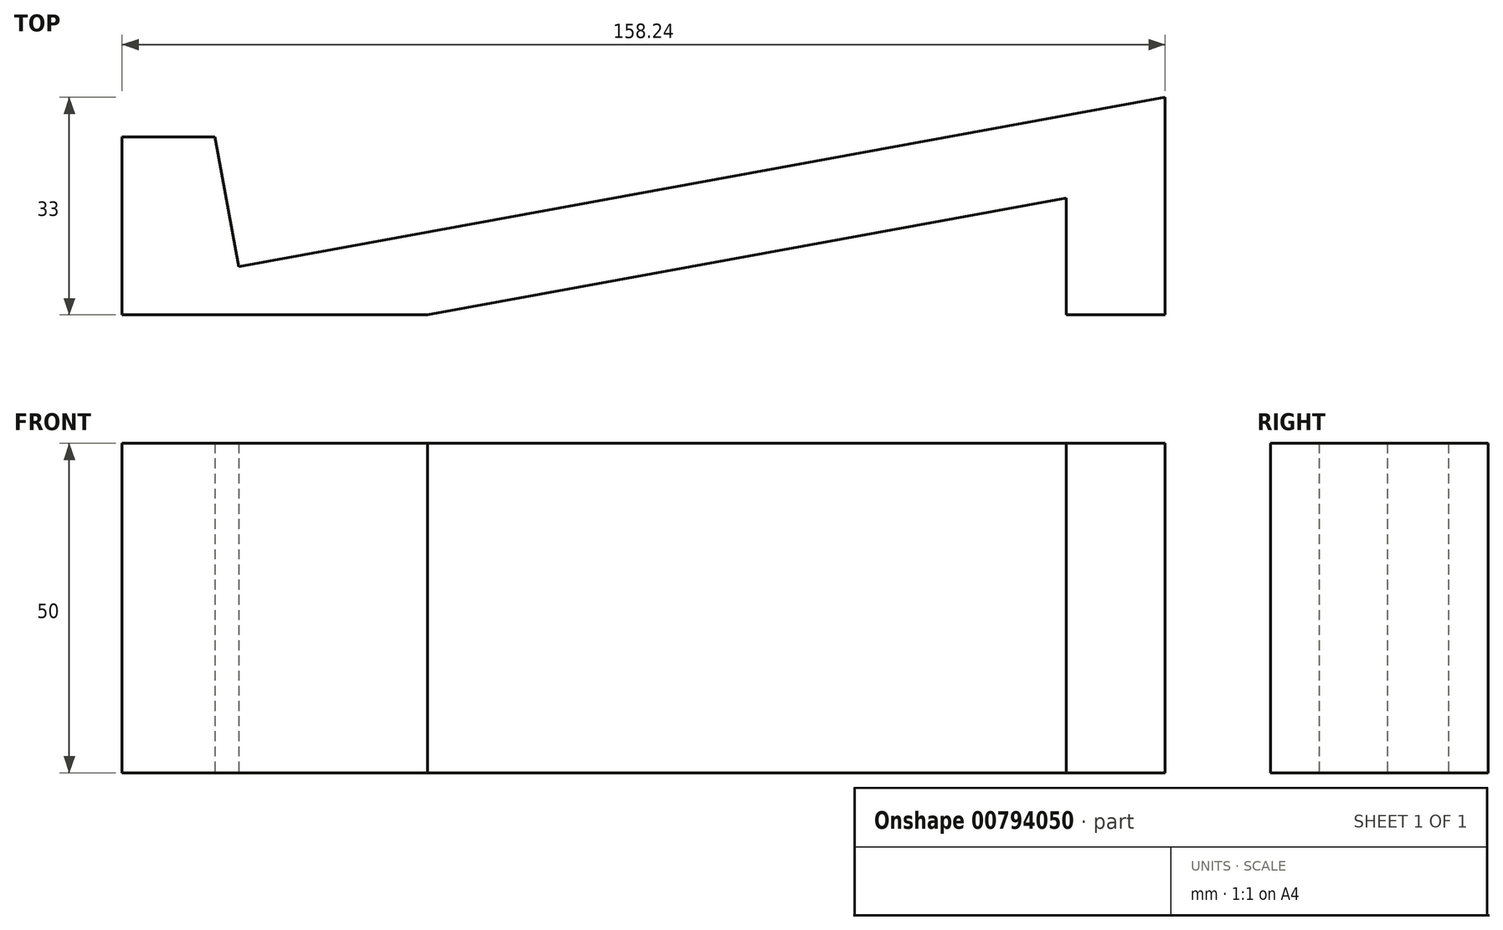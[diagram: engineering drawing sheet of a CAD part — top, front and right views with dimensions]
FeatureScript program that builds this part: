
annotation { "Feature Type Name" : "Feature", "Feature Type Description" : "" }
export const myFeature = defineFeature(function(context is Context, id is Id, definition is map)
    precondition{}
    {
        {
            var Q0;
            Q0=qCreatedBy(makeId("Top.planeOp"),FACE);
            var sketch = newSketch(context, id + "F0", { "sketchPlane" : qUnion([Q0])});
            skLineSegment(sketch, "E0", {"start": v(-66, 0) * mm, "end": v(-19.65, 0) * mm});
            skLineSegment(sketch, "E1", {"start": v(92.24, 0) * mm, "end": v(92.24, 33) * mm});
            skLineSegment(sketch, "E2", {"start": v(92.24, 33) * mm, "end": v(-48.3, 7.33) * mm});
            skLineSegment(sketch, "E3", {"start": v(-48.3, 7.33) * mm, "end": v(-51.9, 27) * mm});
            skLineSegment(sketch, "E4", {"start": v(-51.9, 27) * mm, "end": v(-66, 27) * mm});
            skLineSegment(sketch, "E5", {"start": v(-66, 27) * mm, "end": v(-66, 0) * mm});
            skLineSegment(sketch, "E6", {"start": v(77.24, 0) * mm, "end": v(77.24, 17.7) * mm});
            skLineSegment(sketch, "E7", {"start": v(77.24, 17.7) * mm, "end": v(-19.65, 0) * mm});
            skLineSegment(sketch, "E8.trimOffspring", {"start": v(77.24, 0) * mm, "end": v(92.24, 0) * mm});
            skSolve(sketch);
        }
        {
            var Q0;
            Q0 = qSketchRegion(id + "F0", true);
            extrude(context, id + "F1", {"entities" : qUnion([Q0]), "depth" : 50 * mm, "offsetDistance" : 25 * mm});
        }
    });
